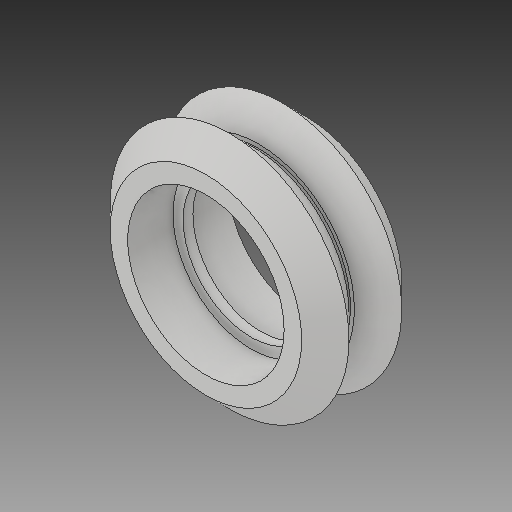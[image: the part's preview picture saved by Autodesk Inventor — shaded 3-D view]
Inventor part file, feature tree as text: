
AUTODESK INVENTOR PART (.ipt)
format: ipt  version: 2018 (Build 220112000, 112)  size: 160,256 bytes
history: native  units: mm
features: sketch x5, other x3
ambient origin geometry x8: Origin, YZ Plane, XZ Plane, XY Plane, X Axis, Y Axis, Z Axis, Center Point
bodies: Solid1 (feature_tree)
feature tree (8):
  other  "dELRIN_MIR1.ipt"
  other  "Solid1::dELRIN_MIR1.ipt"
  other  "TaggingFeature1"
  sketch  "Sketch1"  dims[d0=10.0mm]
  sketch  "Sketch2"
  sketch  "Sketch3"
  sketch  "Sketch4"
  sketch  "Sketch5"
